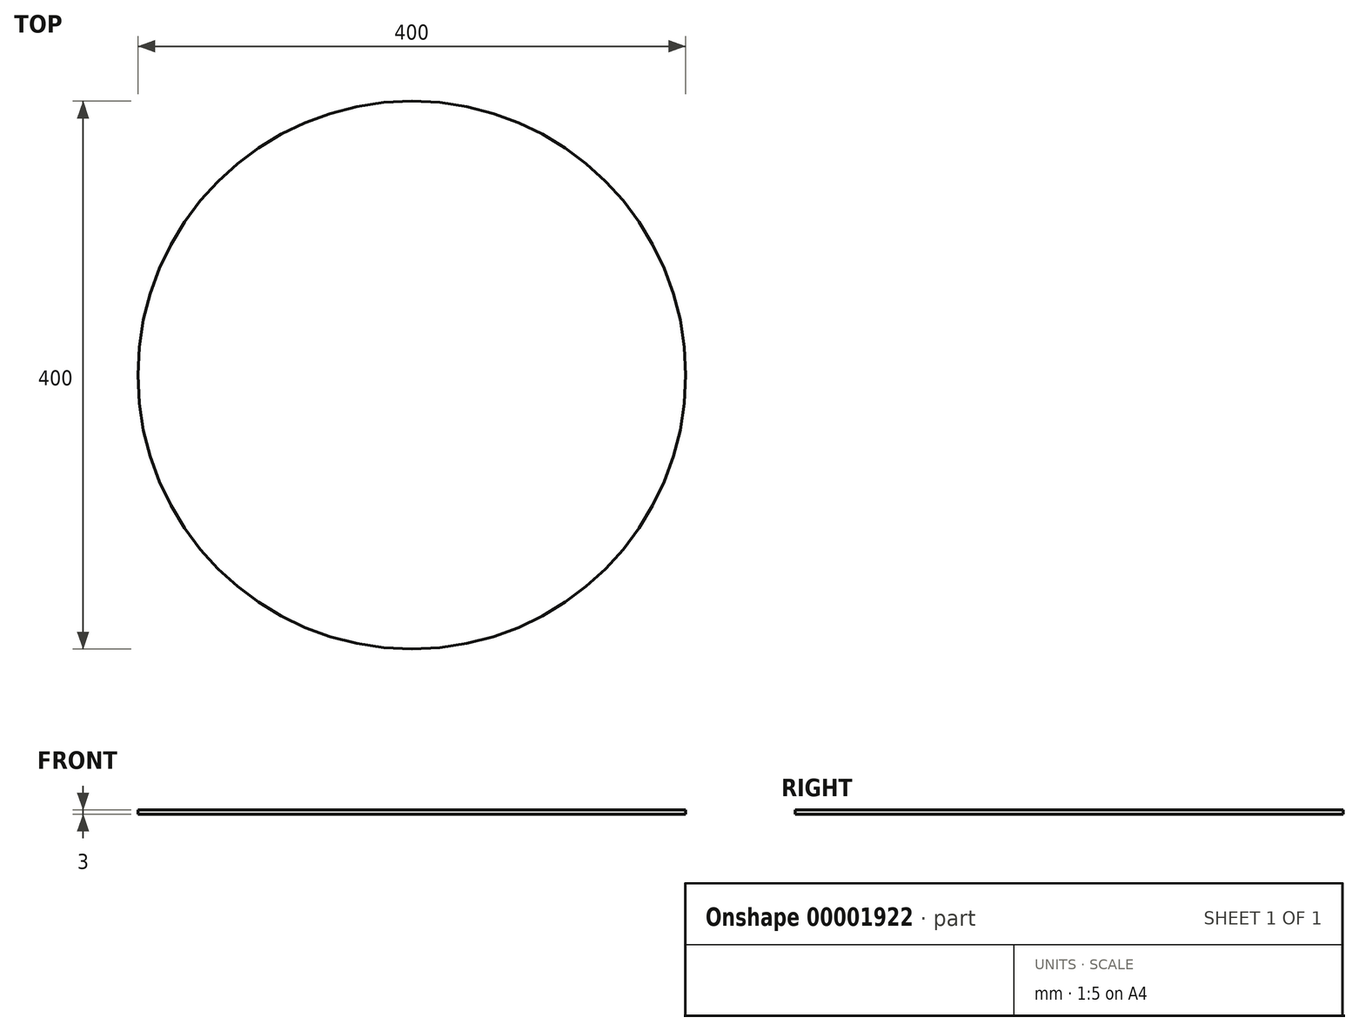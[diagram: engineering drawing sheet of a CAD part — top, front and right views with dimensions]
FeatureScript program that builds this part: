
annotation { "Feature Type Name" : "Feature", "Feature Type Description" : "" }
export const myFeature = defineFeature(function(context is Context, id is Id, definition is map)
    precondition{}
    {
        {
            var Q0;
            Q0=qCreatedBy(makeId("Top.planeOp"),FACE);
            var sketch = newSketch(context, id + "F0", { "sketchPlane" : qUnion([Q0])});
            skCircle(sketch, "E0", {"center": v(0, 0) * mm, "radius": 200 * mm});
            skPoint(sketch, "E1", {"position": v(-200, 0) * mm});
            skSolve(sketch);
        }
        {
            var Q0;
            Q0=makeQuery(id+"F0.imprint","IMPRINT",FACE,{"disambiguationData":[TD([[makeQuery(id+"F0.imprint","IMPRINT",EDGE,{"derivedFrom":sQuery(id+"F0.wireOp",EDGE,"E0")}),1.0]])]});
            extrude(context, id + "F1", {"entities" : qUnion([Q0]), "oppositeDirection" : true, "depth" : 3 * mm});
        }
        {
            var Q0;
            Q0=qCreatedBy(makeId("Front.planeOp"),FACE);
            var sketch = newSketch(context, id + "F2", { "sketchPlane" : qUnion([Q0])});
            skFitSpline(sketch, "E2", {"points": [v(-200, 0) * mm, v(-320, 300) * mm, v(-310, 710) * mm, v(-200, 800) * mm], "startDerivative": vector(-351.52, 0) * mm, "endDerivative": vector(630.97, 0) * mm});
            skLineSegment(sketch, "E3", {"start": v(-200, 1129.93) * mm, "end": v(-200, -145.67) * mm, "construction": true});
            skLineSegment(sketch, "E4", {"start": v(0, -182.47) * mm, "end": v(0, 944.62) * mm, "construction": true});
            skLineSegment(sketch, "E5", {"start": v(-200, 800) * mm, "end": v(0, 800) * mm});
            skLineSegment(sketch, "E6", {"start": v(-452.95, 0) * mm, "end": v(256.45, 0) * mm, "construction": true});
            skLineSegment(sketch, "E7", {"start": v(-200, 800) * mm, "end": v(-368.33, 800) * mm, "construction": true});
            skSolve(sketch);
        }
        {
            var Q0;
            Q0=qCreatedBy(makeId("Front.planeOp"),FACE);
            var sketch = newSketch(context, id + "F3", { "sketchPlane" : qUnion([Q0])});
            skLineSegment(sketch, "E8", {"start": v(0, 815) * mm, "end": v(-140, 815) * mm});
            skLineSegment(sketch, "E9", {"start": v(0, 995) * mm, "end": v(214.22, 995) * mm, "construction": true});
            skFitSpline(sketch, "E10", {"points": [v(-140, 815) * mm, v(-210.31, 889.02) * mm, v(-138.2, 969.86) * mm, v(0, 995) * mm], "startDerivative": vector(-470.67, 0) * mm, "endDerivative": vector(424.5, 0) * mm});
            skLineSegment(sketch, "E11", {"start": v(140.05, 815) * mm, "end": v(-322.2, 815) * mm, "construction": true});
            skLineSegment(sketch, "E12", {"start": v(0, 995) * mm, "end": v(-260.6, 995) * mm, "construction": true});
            skLineSegment(sketch, "E13", {"start": v(-210.31, 1125) * mm, "end": v(-210.31, 511.36) * mm, "construction": true});
            skFitSpline(sketch, "E14", {"points": [v(-156.27, 816.59) * mm, v(-154.9, 800.08) * mm], "startDerivative": vector(7, -17.3) * mm, "endDerivative": vector(-3.54, -16.11) * mm});
            skSolve(sketch);
        }
        {
            var Q0;
            Q0=sQuery(id+"F3.wireOp",EDGE,"E10");
            var Q1;
            Q1=sQuery(id+"F3.wireOp",EDGE,"E8");
            var Q2;
            Q2=sQuery(id+"F2.wireOp",EDGE,"E4");
            revolve(context, id + "F4", {"bodyType" : ToolBodyType.SURFACE, "surfaceEntities" : qUnion([Q0, Q1]), "axis" : qUnion([Q2]), "revolveType" : RevolveType.FULL});
        }
        {
            var Q0;
            Q0=sQuery(id+"F2.wireOp",EDGE,"E5");
            var Q1;
            Q1=sQuery(id+"F2.wireOp",EDGE,"E2");
            var Q2;
            Q2=sQuery(id+"F2.wireOp",EDGE,"E4");
            revolve(context, id + "F5", {"bodyType" : ToolBodyType.SURFACE, "surfaceEntities" : qUnion([Q0, Q1]), "axis" : qUnion([Q2]), "revolveType" : RevolveType.FULL});
        }
        {
            var Q0;
            Q0=sQuery(id+"F3.wireOp",EDGE,"E14");
            var Q1;
            Q1=sQuery(id+"F2.wireOp",EDGE,"E4");
            revolve(context, id + "F6", {"bodyType" : ToolBodyType.SURFACE, "surfaceEntities" : qUnion([Q0]), "axis" : qUnion([Q1]), "revolveType" : RevolveType.FULL});
        }
    });
